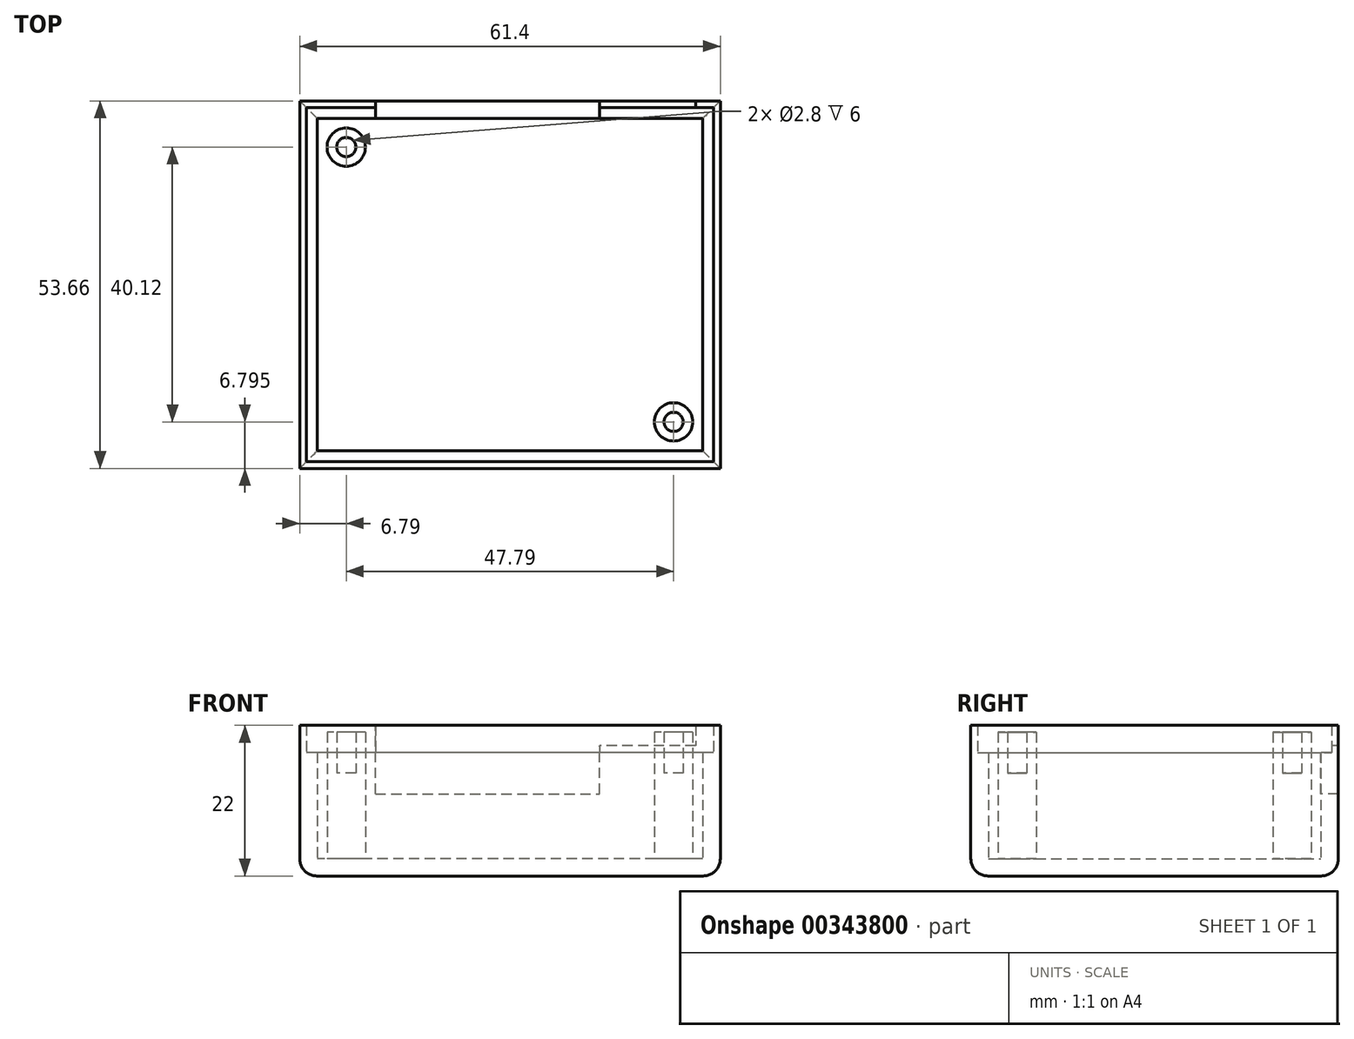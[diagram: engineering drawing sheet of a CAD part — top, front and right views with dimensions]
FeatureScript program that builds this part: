
annotation { "Feature Type Name" : "Feature", "Feature Type Description" : "" }
export const myFeature = defineFeature(function(context is Context, id is Id, definition is map)
    precondition{}
    {
        {
            var Q0;
            Q0=qCreatedBy(makeId("Top.planeOp"),FACE);
            var sketch = newSketch(context, id + "F0", { "sketchPlane" : qUnion([Q0])});
            skLineSegment(sketch, "E0.bottom", {"start": v(26.9, -23.02) * mm, "end": v(-26.9, -23.03) * mm, "construction": true});
            skLineSegment(sketch, "E0.top", {"start": v(26.9, 23.03) * mm, "end": v(-26.9, 23.02) * mm, "construction": true});
            skLineSegment(sketch, "E0.left", {"start": v(26.9, -23.02) * mm, "end": v(26.9, 23.03) * mm, "construction": true});
            skLineSegment(sketch, "E0.right", {"start": v(-26.9, -23.03) * mm, "end": v(-26.9, 23.03) * mm, "construction": true});
            skPoint(sketch, "E0.middle", {"position": v(0, 0) * mm});
            skCircle(sketch, "E1", {"center": v(23.88, -20.03) * mm, "radius": 1.4 * mm});
            skCircle(sketch, "E2", {"center": v(-23.91, 20.09) * mm, "radius": 1.4 * mm});
            skCircle(sketch, "E3", {"center": v(23.88, -20.03) * mm, "radius": 2.8 * mm});
            skCircle(sketch, "E4", {"center": v(-23.91, 20.09) * mm, "radius": 2.8 * mm});
            skLineSegment(sketch, "E5.0", {"start": v(28.15, -24.27) * mm, "end": v(-28.15, -24.28) * mm});
            skLineSegment(sketch, "E5.1", {"start": v(28.15, -24.27) * mm, "end": v(28.15, 24.28) * mm});
            skLineSegment(sketch, "E5.2", {"start": v(28.15, 24.28) * mm, "end": v(-28.15, 24.28) * mm});
            skLineSegment(sketch, "E5.3", {"start": v(-28.15, -24.28) * mm, "end": v(-28.15, 24.28) * mm});
            skLineSegment(sketch, "E6.0", {"start": v(29.7, 25.83) * mm, "end": v(-29.7, 25.82) * mm});
            skLineSegment(sketch, "E6.1", {"start": v(29.7, -25.82) * mm, "end": v(29.7, 25.83) * mm});
            skLineSegment(sketch, "E6.2", {"start": v(29.7, -25.82) * mm, "end": v(-29.7, -25.83) * mm});
            skLineSegment(sketch, "E6.3", {"start": v(-29.7, -25.83) * mm, "end": v(-29.7, 25.82) * mm});
            skLineSegment(sketch, "E7.0", {"start": v(30.7, 26.83) * mm, "end": v(-30.7, 26.83) * mm});
            skLineSegment(sketch, "E7.1", {"start": v(30.7, -26.82) * mm, "end": v(30.7, 26.83) * mm});
            skLineSegment(sketch, "E7.2", {"start": v(30.7, -26.82) * mm, "end": v(-30.7, -26.83) * mm});
            skLineSegment(sketch, "E7.3", {"start": v(-30.7, -26.83) * mm, "end": v(-30.7, 26.82) * mm});
            skLineSegment(sketch, "E8", {"start": v(26.9, 23.03) * mm, "end": v(26.9, 24.28) * mm, "construction": true});
            skSolve(sketch);
        }
        {
            var Q0;
            Q0=makeQuery(id+"F0.imprint","IMPRINT",FACE,{"disambiguationData":[TD([[makeQuery(id+"F0.imprint","IMPRINT",EDGE,{"derivedFrom":sQuery(id+"F0.wireOp",EDGE,"E3")}),-1.0]])]});
            extrude(context, id + "F1", {"entities" : qUnion([Q0]), "depth" : 2.5 * mm});
        }
        {
            var Q0;
            Q0=makeQuery(id+"F0.imprint","IMPRINT",FACE,{"disambiguationData":[TD([[makeQuery(id+"F0.imprint","IMPRINT",EDGE,{"derivedFrom":sQuery(id+"F0.wireOp",EDGE,"E5.0")}),1.0]])]});
            extrude(context, id + "F2", {"entities" : qUnion([Q0]), "operationType" : NewBodyOperationType.ADD, "depth" : 18 * mm});
        }
        {
            var Q0;
            Q0=makeQuery(id+"F0.imprint","IMPRINT",FACE,{"disambiguationData":[TD([[makeQuery(id+"F0.imprint","IMPRINT",EDGE,{"derivedFrom":sQuery(id+"F0.wireOp",EDGE,"E6.0")}),-1.0]])]});
            extrude(context, id + "F3", {"entities" : qUnion([Q0]), "operationType" : NewBodyOperationType.ADD, "depth" : 22 * mm});
        }
        {
            var Q0;
            Q0=makeQuery(id+"F0.imprint","IMPRINT",FACE,{"disambiguationData":[TD([[makeQuery(id+"F0.imprint","IMPRINT",EDGE,{"derivedFrom":sQuery(id+"F0.wireOp",EDGE,"E2")}),-1.0]])]});
            var Q1;
            Q1=makeQuery(id+"F0.imprint","IMPRINT",FACE,{"disambiguationData":[TD([[makeQuery(id+"F0.imprint","IMPRINT",EDGE,{"derivedFrom":sQuery(id+"F0.wireOp",EDGE,"E1")}),-1.0]])]});
            extrude(context, id + "F4", {"entities" : qUnion([Q0, Q1]), "operationType" : NewBodyOperationType.ADD, "depth" : 21 * mm});
        }
        {
            var Q0;
            Q0=makeQuery(id+"F0.imprint","IMPRINT",FACE,{"disambiguationData":[TD([[makeQuery(id+"F0.imprint","IMPRINT",EDGE,{"derivedFrom":sQuery(id+"F0.wireOp",EDGE,"E1")}),1.0]])]});
            var Q1;
            Q1=makeQuery(id+"F0.imprint","IMPRINT",FACE,{"disambiguationData":[TD([[makeQuery(id+"F0.imprint","IMPRINT",EDGE,{"derivedFrom":sQuery(id+"F0.wireOp",EDGE,"E2")}),1.0]])]});
            extrude(context, id + "F5", {"entities" : qUnion([Q0, Q1]), "operationType" : NewBodyOperationType.ADD, "depth" : 15 * mm, "offsetDistance" : 25 * mm});
        }
        {
            var Q0;
            Q0=makeQuery(id+"F3.opExtrude","CAP_EDGE",EDGE,{"disambiguationData":[OSD([sQuery(id+"F0.wireOp",EDGE,"E7.2")])],"isStart":true});
            var Q1;
            Q1=makeQuery(id+"F3.opExtrude","CAP_EDGE",EDGE,{"disambiguationData":[OSD([sQuery(id+"F0.wireOp",EDGE,"E7.1")])],"isStart":true});
            var Q2;
            Q2=makeQuery(id+"F3.opExtrude","CAP_EDGE",EDGE,{"disambiguationData":[OSD([sQuery(id+"F0.wireOp",EDGE,"E7.3")])],"isStart":true});
            var Q3;
            Q3=makeQuery(id+"F3.opExtrude","CAP_EDGE",EDGE,{"disambiguationData":[OSD([sQuery(id+"F0.wireOp",EDGE,"E7.0")])],"isStart":true});
            var Q4;
            Q4=makeQuery(id+"F1.opExtrude","CAP_EDGE",EDGE,{"disambiguationData":[OSD([sQuery(id+"F0.wireOp",EDGE,"E5.1")])],"isStart":false});
            var Q5;
            Q5=makeQuery(id+"F1.opExtrude","CAP_EDGE",EDGE,{"disambiguationData":[OSD([sQuery(id+"F0.wireOp",EDGE,"E5.2")])],"isStart":false});
            var Q6;
            Q6=makeQuery(id+"F1.opExtrude","CAP_EDGE",EDGE,{"disambiguationData":[OSD([sQuery(id+"F0.wireOp",EDGE,"E5.0")])],"isStart":false});
            var Q7;
            Q7=makeQuery(id+"F1.opExtrude","CAP_EDGE",EDGE,{"disambiguationData":[OSD([sQuery(id+"F0.wireOp",EDGE,"E5.3")])],"isStart":false});
            fillet(context, id + "F6", {"entities" : qUnion([Q0, Q1, Q2, Q3, Q4, Q5, Q6, Q7]), "radius" : 2.5 * mm, "tangentPropagation" : true, "allowEdgeOverflow" : false});
        }
        {
            var Q0;
            Q0=makeQuery(id+"F3.opExtrude","CAP_FACE",FACE,{"disambiguationData":[OSD([sQuery(id+"F0.wireOp",EDGE,"E6.0"),sQuery(id+"F0.wireOp",EDGE,"E6.1"),sQuery(id+"F0.wireOp",EDGE,"E6.2"),sQuery(id+"F0.wireOp",EDGE,"E6.3"),sQuery(id+"F0.wireOp",EDGE,"E7.0"),sQuery(id+"F0.wireOp",EDGE,"E7.1"),sQuery(id+"F0.wireOp",EDGE,"E7.2"),sQuery(id+"F0.wireOp",EDGE,"E7.3")])],"isStart":false});
            var sketch = newSketch(context, id + "F7", { "sketchPlane" : qUnion([Q0])});
            skLineSegment(sketch, "E9", {"start": v(27.1, 26.83) * mm, "end": v(27.1, 24.28) * mm});
            skLineSegment(sketch, "E10", {"start": v(27.1, 26.83) * mm, "end": v(-19.65, 26.83) * mm});
            skLineSegment(sketch, "E11", {"start": v(-19.65, 26.83) * mm, "end": v(-19.65, 24.28) * mm});
            skLineSegment(sketch, "E12", {"start": v(-19.65, 24.28) * mm, "end": v(27.1, 24.28) * mm});
            skLineSegment(sketch, "E13", {"start": v(13.1, 26.83) * mm, "end": v(13.1, 24.28) * mm});
            skSolve(sketch);
        }
        {
            var Q0;
            {var subQ1=sQuery(id+"F7.wireOp",EDGE,"E10");var subQ3=sQuery(id+"F7.wireOp",EDGE,"E13");var subQ4=makeQuery(id+"F7.imprint","INTERSECT",VERTEX,{"derivedFrom":[subQ1,subQ3]});Q0=makeQuery(id+"F7.imprint","IMPRINT",FACE,{"disambiguationData":[TD([[makeQuery(id+"F7.imprint","IMPRINT",EDGE,{"disambiguationData":[TD([[subQ4,-1.0]])],"derivedFrom":subQ3}),-1.0]])]});}
            var Q1;
            {var subQ0=sQuery(id+"F7.wireOp",EDGE,"E12");var subQ1=sQuery(id+"F7.wireOp",EDGE,"E11");var subQ2=makeQuery(id+"F7.imprint","INTERSECT",VERTEX,{"derivedFrom":[subQ1,subQ0]});Q1=makeQuery(id+"F7.imprint","IMPRINT",FACE,{"disambiguationData":[TD([[makeQuery(id+"F7.imprint","IMPRINT",EDGE,{"disambiguationData":[TD([[subQ2,1.0]])],"derivedFrom":subQ1}),1.0]])]});}
            extrude(context, id + "F8", {"entities" : qUnion([Q0, Q1]), "operationType" : NewBodyOperationType.REMOVE, "oppositeDirection" : true, "depth" : 10 * mm});
        }
        {
            var Q0;
            {var subQ0=sQuery(id+"F7.wireOp",EDGE,"E10");var subQ5=sQuery(id+"F7.wireOp",EDGE,"E13");var subQ7=makeQuery(id+"F7.imprint","INTERSECT",VERTEX,{"derivedFrom":[subQ0,subQ5]});Q0=makeQuery(id+"F7.imprint","IMPRINT",FACE,{"disambiguationData":[TD([[makeQuery(id+"F7.imprint","IMPRINT",EDGE,{"disambiguationData":[TD([[subQ7,-1.0]])],"derivedFrom":subQ5}),1.0]])]});}
            var Q1;
            {var subQ0=sQuery(id+"F7.wireOp",EDGE,"E12");var subQ1=sQuery(id+"F7.wireOp",EDGE,"E9");var subQ2=makeQuery(id+"F7.imprint","INTERSECT",VERTEX,{"derivedFrom":[subQ1,subQ0]});Q1=makeQuery(id+"F7.imprint","IMPRINT",FACE,{"disambiguationData":[TD([[makeQuery(id+"F7.imprint","IMPRINT",EDGE,{"disambiguationData":[TD([[subQ2,1.0]])],"derivedFrom":subQ1}),-1.0]])]});}
            extrude(context, id + "F9", {"entities" : qUnion([Q0, Q1]), "operationType" : NewBodyOperationType.REMOVE, "oppositeDirection" : true, "depth" : 3 * mm});
        }
    });
